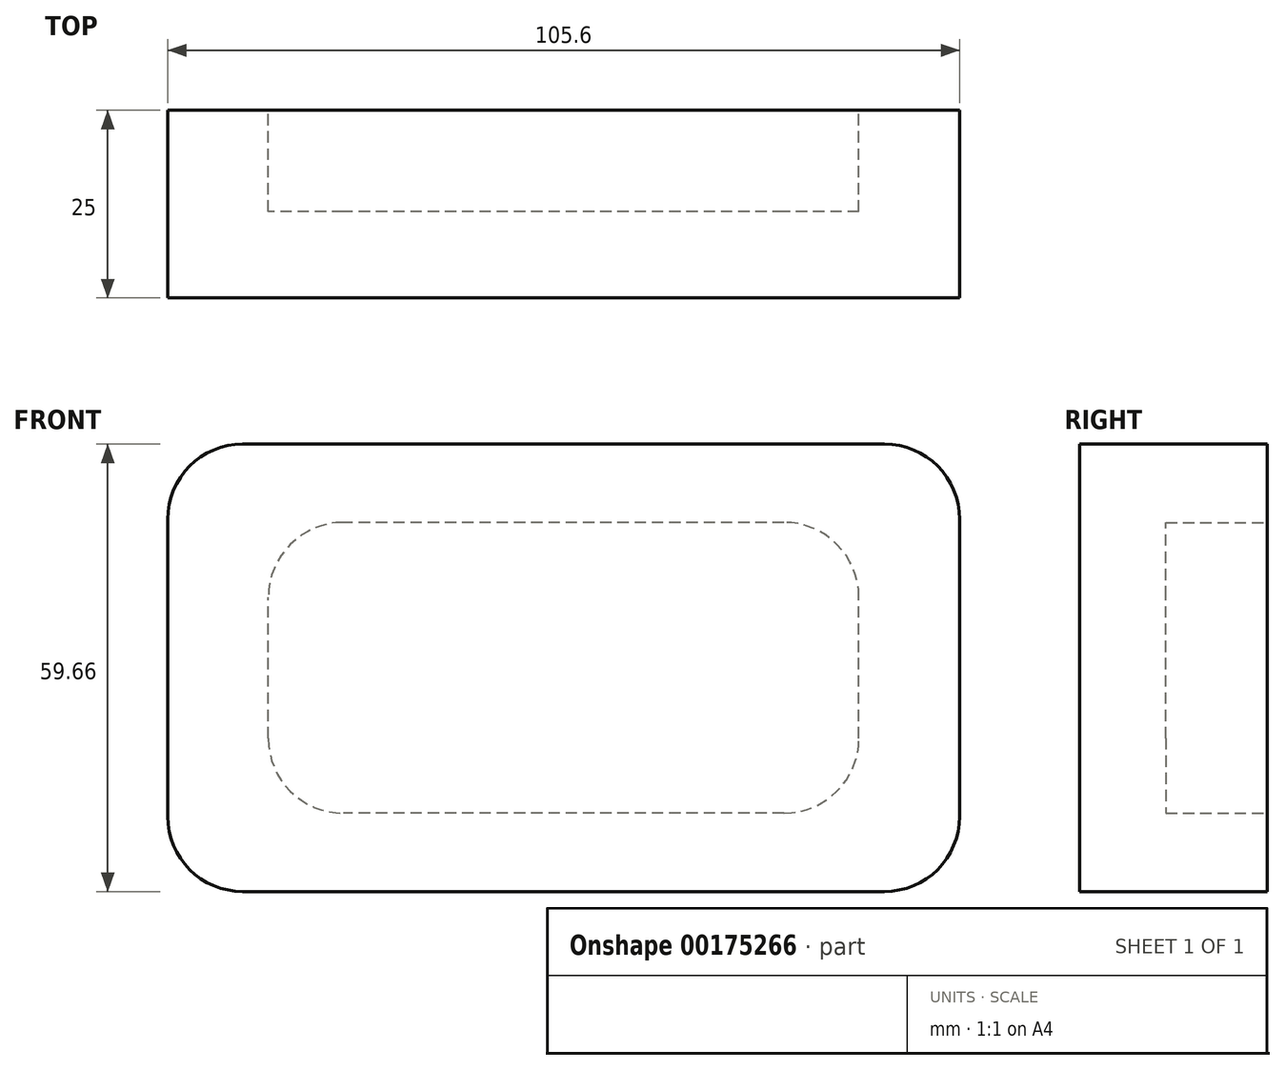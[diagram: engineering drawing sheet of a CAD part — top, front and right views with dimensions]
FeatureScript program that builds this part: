
annotation { "Feature Type Name" : "Feature", "Feature Type Description" : "" }
export const myFeature = defineFeature(function(context is Context, id is Id, definition is map)
    precondition{}
    {
        {
            var Q0;
            Q0=qCreatedBy(makeId("Front.planeOp"),FACE);
            var sketch = newSketch(context, id + "F0", { "sketchPlane" : qUnion([Q0])});
            skLineSegment(sketch, "E0.bottom", {"start": v(-42.8, -29.83) * mm, "end": v(42.8, -29.83) * mm});
            skLineSegment(sketch, "E0.top", {"start": v(-42.8, 29.83) * mm, "end": v(42.8, 29.83) * mm});
            skLineSegment(sketch, "E0.left", {"start": v(-52.8, -19.83) * mm, "end": v(-52.8, 19.83) * mm});
            skLineSegment(sketch, "E0.right", {"start": v(52.8, -19.83) * mm, "end": v(52.8, 19.83) * mm});
            skPoint(sketch, "E0.middle", {"position": v(0, 0) * mm});
            skPoint(sketch, "E1.visualSharp", {"position": v(-52.8, 29.83) * mm});
            skArc(sketch, "E1.filletArc", {"start": v(-42.8, 29.83) * mm, "mid": v(-49.87, 26.9) * mm, "end": v(-52.8, 19.83) * mm});
            skPoint(sketch, "E2.visualSharp", {"position": v(52.8, 29.83) * mm});
            skArc(sketch, "E2.filletArc", {"start": v(52.8, 19.83) * mm, "mid": v(49.87, 26.9) * mm, "end": v(42.8, 29.83) * mm});
            skPoint(sketch, "E3.visualSharp", {"position": v(52.8, -29.83) * mm});
            skArc(sketch, "E3.filletArc", {"start": v(42.8, -29.83) * mm, "mid": v(49.87, -26.9) * mm, "end": v(52.8, -19.83) * mm});
            skPoint(sketch, "E4.visualSharp", {"position": v(-52.8, -29.83) * mm});
            skArc(sketch, "E4.filletArc", {"start": v(-52.8, -19.83) * mm, "mid": v(-49.87, -26.9) * mm, "end": v(-42.8, -29.83) * mm});
            skSolve(sketch);
        }
        {
            var Q0;
            Q0=makeQuery(id+"F0.imprint","IMPRINT",FACE,{"disambiguationData":[TD([[makeQuery(id+"F0.imprint","IMPRINT",EDGE,{"derivedFrom":sQuery(id+"F0.wireOp",EDGE,"E0.bottom")}),1.0]])]});
            extrude(context, id + "F1", {"entities" : qUnion([Q0]), "depth" : 25 * mm});
        }
        {
            var Q0;
            Q0=makeQuery(id+"F1.opExtrude","CAP_FACE",FACE,{"disambiguationData":[OSD([sQuery(id+"F0.wireOp",EDGE,"E0.bottom"),sQuery(id+"F0.wireOp",EDGE,"E0.top"),sQuery(id+"F0.wireOp",EDGE,"E0.left"),sQuery(id+"F0.wireOp",EDGE,"E0.right"),sQuery(id+"F0.wireOp",EDGE,"E1.filletArc"),sQuery(id+"F0.wireOp",EDGE,"E2.filletArc"),sQuery(id+"F0.wireOp",EDGE,"E3.filletArc"),sQuery(id+"F0.wireOp",EDGE,"E4.filletArc")])],"isStart":true});
            var sketch = newSketch(context, id + "F2", { "sketchPlane" : qUnion([Q0])});
            skLineSegment(sketch, "E5.bottom", {"start": v(-29.38, -19.39) * mm, "end": v(29.38, -19.39) * mm});
            skLineSegment(sketch, "E5.top", {"start": v(-29.38, 19.39) * mm, "end": v(29.38, 19.39) * mm});
            skLineSegment(sketch, "E5.left", {"start": v(-39.38, -9.39) * mm, "end": v(-39.38, 9.39) * mm});
            skLineSegment(sketch, "E5.right", {"start": v(39.38, -9.39) * mm, "end": v(39.38, 9.39) * mm});
            skPoint(sketch, "E5.middle", {"position": v(0, 0) * mm});
            skPoint(sketch, "E6.visualSharp", {"position": v(-39.38, 19.39) * mm});
            skArc(sketch, "E6.filletArc", {"start": v(-29.38, 19.39) * mm, "mid": v(-36.45, 16.46) * mm, "end": v(-39.38, 9.39) * mm});
            skPoint(sketch, "E7.visualSharp", {"position": v(-39.38, -19.39) * mm});
            skArc(sketch, "E7.filletArc", {"start": v(-39.38, -9.39) * mm, "mid": v(-36.45, -16.46) * mm, "end": v(-29.38, -19.39) * mm});
            skPoint(sketch, "E8.visualSharp", {"position": v(39.38, -19.39) * mm});
            skArc(sketch, "E8.filletArc", {"start": v(29.38, -19.39) * mm, "mid": v(36.45, -16.46) * mm, "end": v(39.38, -9.39) * mm});
            skPoint(sketch, "E9.visualSharp", {"position": v(39.38, 19.39) * mm});
            skArc(sketch, "E9.filletArc", {"start": v(39.38, 9.39) * mm, "mid": v(36.45, 16.46) * mm, "end": v(29.38, 19.39) * mm});
            skSolve(sketch);
        }
        {
            var Q0;
            Q0=makeQuery(id+"F2.imprint","IMPRINT",FACE,{"disambiguationData":[TD([[makeQuery(id+"F2.imprint","IMPRINT",EDGE,{"derivedFrom":sQuery(id+"F2.wireOp",EDGE,"E5.bottom")}),1.0]])]});
            extrude(context, id + "F3", {"entities" : qUnion([Q0]), "operationType" : NewBodyOperationType.REMOVE, "oppositeDirection" : true, "depth" : 13.5 * mm});
        }
    });
